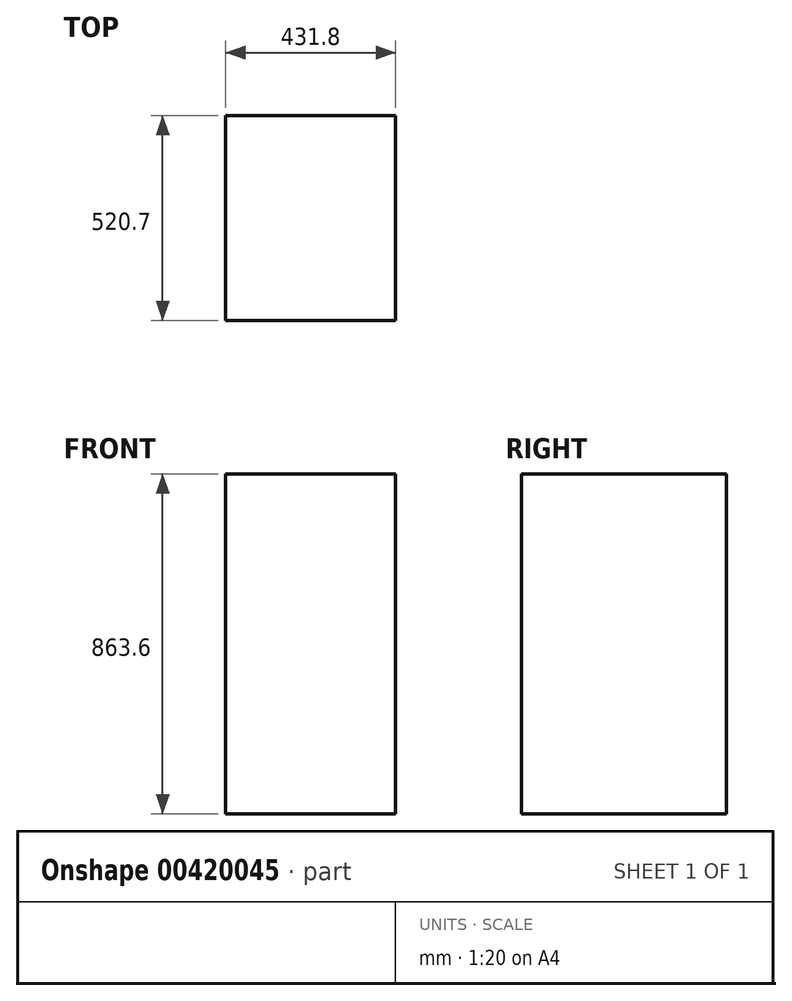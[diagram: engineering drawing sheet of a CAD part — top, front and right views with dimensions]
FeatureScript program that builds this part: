
annotation { "Feature Type Name" : "Feature", "Feature Type Description" : "" }
export const myFeature = defineFeature(function(context is Context, id is Id, definition is map)
    precondition{}
    {
        {
            var Q0;
            Q0=qCreatedBy(makeId("Front.planeOp"),FACE);
            var sketch = newSketch(context, id + "F0", { "sketchPlane" : qUnion([Q0])});
            skLineSegment(sketch, "E0.bottom", {"start": v(0, 0) * mm, "end": v(431.8, 0) * mm});
            skLineSegment(sketch, "E0.top", {"start": v(0, 863.6) * mm, "end": v(431.8, 863.6) * mm});
            skLineSegment(sketch, "E0.left", {"start": v(0, 0) * mm, "end": v(0, 863.6) * mm});
            skLineSegment(sketch, "E0.right", {"start": v(431.8, 0) * mm, "end": v(431.8, 863.6) * mm});
            skSolve(sketch);
        }
        {
            var Q0;
            Q0=makeQuery(id+"F0.imprint","IMPRINT",FACE,{"disambiguationData":[TD([[makeQuery(id+"F0.imprint","IMPRINT",EDGE,{"derivedFrom":sQuery(id+"F0.wireOp",EDGE,"E0.bottom")}),1.0]])]});
            extrude(context, id + "F1", {"entities" : qUnion([Q0]), "depth" : 520.7 * mm});
        }
    });
